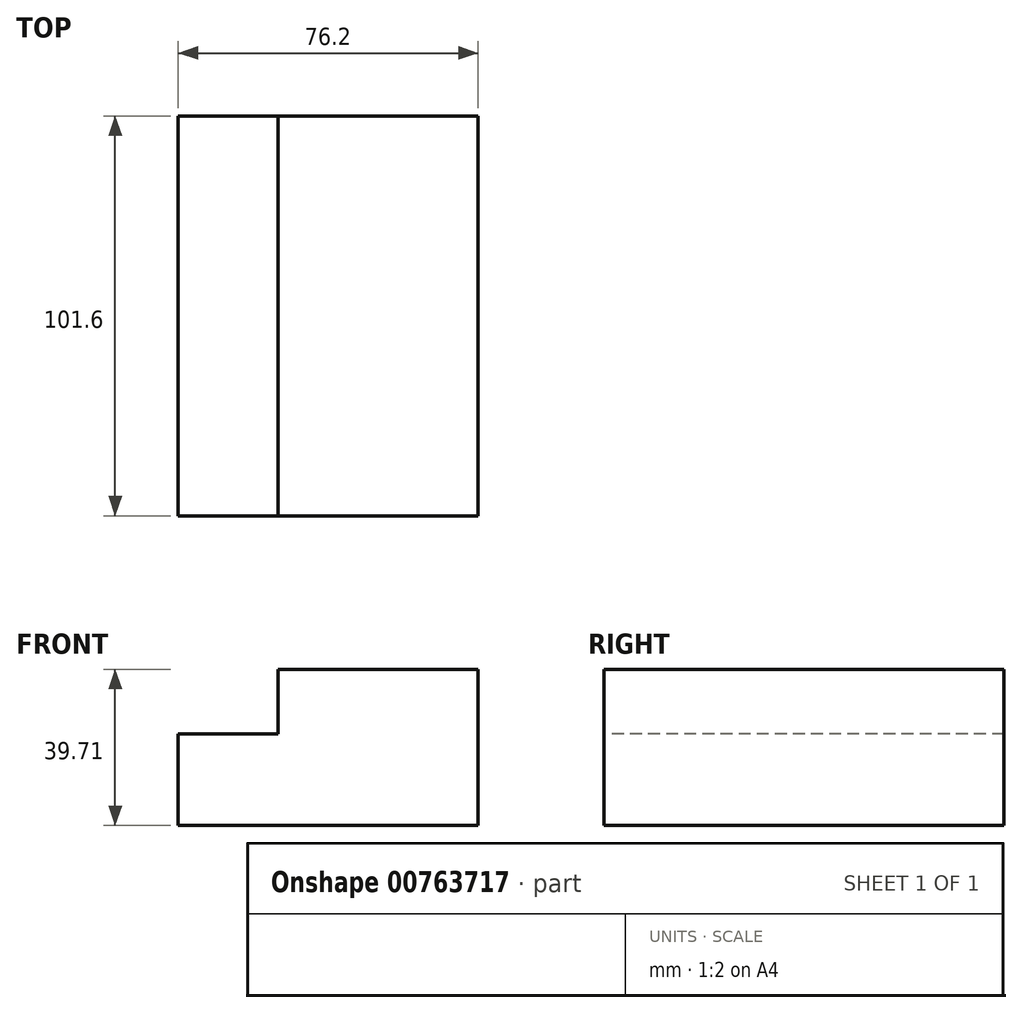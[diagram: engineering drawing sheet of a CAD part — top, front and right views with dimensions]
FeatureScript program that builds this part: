
annotation { "Feature Type Name" : "Feature", "Feature Type Description" : "" }
export const myFeature = defineFeature(function(context is Context, id is Id, definition is map)
    precondition{}
    {
        {
            var Q0;
            Q0=qCreatedBy(makeId("Front.planeOp"),FACE);
            var sketch = newSketch(context, id + "F0", { "sketchPlane" : qUnion([Q0])});
            skLineSegment(sketch, "E0", {"start": v(0, 0) * mm, "end": v(0, 23.3) * mm});
            skLineSegment(sketch, "E1", {"start": v(0, 23.3) * mm, "end": v(25.4, 23.3) * mm});
            skLineSegment(sketch, "E2", {"start": v(25.4, 23.3) * mm, "end": v(25.4, 39.71) * mm});
            skLineSegment(sketch, "E3", {"start": v(25.4, 39.71) * mm, "end": v(76.2, 39.71) * mm});
            skLineSegment(sketch, "E4", {"start": v(76.2, 39.71) * mm, "end": v(76.2, 0) * mm});
            skLineSegment(sketch, "E5", {"start": v(76.2, 0) * mm, "end": v(0, 0) * mm});
            skSolve(sketch);
        }
        {
            var Q0;
            Q0=makeQuery(id+"F0.imprint","IMPRINT",FACE,{"disambiguationData":[TD([[makeQuery(id+"F0.imprint","IMPRINT",EDGE,{"derivedFrom":sQuery(id+"F0.wireOp",EDGE,"E0")}),-1.0]])]});
            extrude(context, id + "F1", {"entities" : qUnion([Q0]), "oppositeDirection" : true, "depth" : 101.6 * mm, "offsetDistance" : 25.4 * mm});
        }
    });
